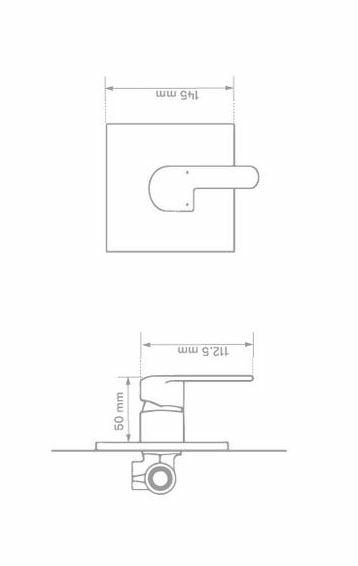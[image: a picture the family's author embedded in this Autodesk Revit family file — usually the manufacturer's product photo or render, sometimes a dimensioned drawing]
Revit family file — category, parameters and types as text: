
# Revit family: 01-0928-11 MEZCLADOR LAVAPLATOS 8 ARCO HELVETIA
name_source: partatom
category: Aparatos sanitarios
revit_build: Autodesk Revit 2018 (Build: 20170223_1515(x64)
units: mm (PartAtom-declared; Revit-internal decimal feet)

## family parameters
Anfitrión = Cara
Compartido = No
Corte con vacíos al cargar = No
Cota de conector redondo = Diámetro de uso
Número OmniClass = 23.31.11.00
Punto de cálculo de habitación = No
Tipo de pieza = Normal

## types (1)
- 01-0928-11
    Alto Aireador = 210 mm
    Alto brazo = 329 mm
    Ancho brazo = 137 mm  [stored 0.449475 ft]
    Ancho entre manijas = 203.2 mm  [stored 0.666667 ft]
    Ancho manija = 70 mm  [stored 0.229659 ft]
    Conexión AC = Sí
    Conexión AF = Sí
    Conexión de residuos = No
    Conexión de ventilación = No
    Descripción = Bimando
    Elevación por defecto = 0 mm  [stored 0 ft]
    Fabricante = Gricol
    Imagen de tipo = <Ninguno>
    Link Ficha Tecnica = http://infotecnica.gricol.com
    Modelo = 01-0928-11
    Plástico - ABS Cromado = Plastico ABS Cromado
    Product Name = MEZCLADOR LAVAPLATOS 8 ARCO HELVETIA
    URL = https://www.gricol.com

note: [stored X ft] marks values corroborated as IEEE doubles in the binary element streams (Revit-internal decimal feet)

## geometry (parser evidence)
native form markers: Blend x2, Sweep x4
no freeform markers — native parametric forms only
